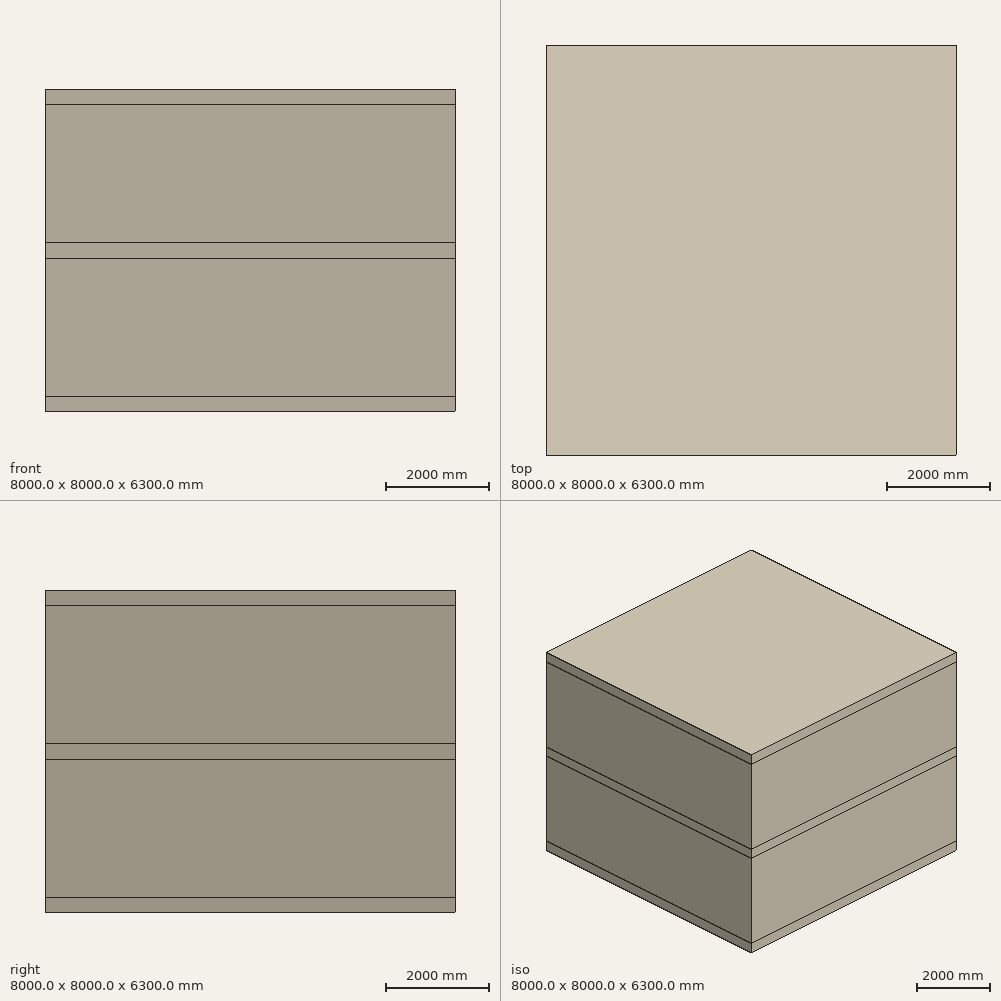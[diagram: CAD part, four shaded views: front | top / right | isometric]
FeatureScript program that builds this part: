
annotation { "Feature Type Name" : "Feature", "Feature Type Description" : "" }
export const myFeature = defineFeature(function(context is Context, id is Id, definition is map)
    precondition{}
    {
        {
            var Q0;
            Q0=qCreatedBy(makeId("Top.planeOp"),FACE);
            var sketch = newSketch(context, id + "F0", { "sketchPlane" : qUnion([Q0])});
            skLineSegment(sketch, "E0.bottom", {"start": v(4000, -4000) * mm, "end": v(-4000, -4000) * mm});
            skLineSegment(sketch, "E0.top", {"start": v(4000, 4000) * mm, "end": v(-4000, 4000) * mm});
            skLineSegment(sketch, "E0.left", {"start": v(4000, -4000) * mm, "end": v(4000, 4000) * mm});
            skLineSegment(sketch, "E0.right", {"start": v(-4000, -4000) * mm, "end": v(-4000, 4000) * mm});
            skPoint(sketch, "E0.middle", {"position": v(0, 0) * mm});
            skSolve(sketch);
        }
        {
            var Q0;
            Q0=qCreatedBy(makeId("Front.planeOp"),FACE);
            var sketch = newSketch(context, id + "F1", { "sketchPlane" : qUnion([Q0])});
            skLineSegment(sketch, "E1.bottom", {"start": v(-4000, 0) * mm, "end": v(4000, 0) * mm, "construction": true});
            skLineSegment(sketch, "E1.top", {"start": v(-4000, 3000) * mm, "end": v(4000, 3000) * mm, "construction": true});
            skLineSegment(sketch, "E1.left", {"start": v(-4000, 0) * mm, "end": v(-4000, 3000) * mm, "construction": true});
            skLineSegment(sketch, "E1.right", {"start": v(4000, 0) * mm, "end": v(4000, 3000) * mm, "construction": true});
            skLineSegment(sketch, "E2.top", {"start": v(-4000, 6000) * mm, "end": v(4000, 6000) * mm, "construction": true});
            skLineSegment(sketch, "E2.left", {"start": v(-4000, 3000) * mm, "end": v(-4000, 6000) * mm, "construction": true});
            skLineSegment(sketch, "E2.right", {"start": v(4000, 3000) * mm, "end": v(4000, 6000) * mm, "construction": true});
            skLineSegment(sketch, "E3.top", {"start": v(-4000, 9000) * mm, "end": v(4000, 9000) * mm, "construction": true});
            skLineSegment(sketch, "E3.left", {"start": v(-4000, 6000) * mm, "end": v(-4000, 9000) * mm, "construction": true});
            skLineSegment(sketch, "E3.right", {"start": v(4000, 6000) * mm, "end": v(4000, 9000) * mm, "construction": true});
            skSolve(sketch);
        }
        {
            var Q0;
            Q0=qCreatedBy(makeId("Top.planeOp"),FACE);
            var Q1;
            Q1=sQuery(id+"F1.wireOp",VERTEX,"E2.left.start");
            cPlane(context, id + "F2", {"entities" : qUnion([Q0, Q1]), "cplaneType" : CPlaneType.PLANE_POINT, "offset" : 25 * mm, "width" : 150 * mm, "height" : 150 * mm});
        }
        {
            var Q0;
            Q0=qCreatedBy(id+"F2.planeOp",FACE);
            var sketch = newSketch(context, id + "F3", { "sketchPlane" : qUnion([Q0])});
            skLineSegment(sketch, "E4.bottom", {"start": v(-4000, 4000) * mm, "end": v(4000, 4000) * mm});
            skLineSegment(sketch, "E4.top", {"start": v(-4000, -4000) * mm, "end": v(4000, -4000) * mm});
            skLineSegment(sketch, "E4.left", {"start": v(-4000, 4000) * mm, "end": v(-4000, -4000) * mm});
            skLineSegment(sketch, "E4.right", {"start": v(4000, 4000) * mm, "end": v(4000, -4000) * mm});
            skSolve(sketch);
        }
        {
            var Q0;
            Q0=qCreatedBy(makeId("Top.planeOp"),FACE);
            var Q1;
            Q1=sQuery(id+"F1.wireOp",VERTEX,"E2.left.end");
            cPlane(context, id + "F4", {"entities" : qUnion([Q0, Q1]), "cplaneType" : CPlaneType.PLANE_POINT, "offset" : 25 * mm, "width" : 150 * mm, "height" : 150 * mm});
        }
        {
            var Q0;
            Q0=qCreatedBy(id+"F4.planeOp",FACE);
            var sketch = newSketch(context, id + "F5", { "sketchPlane" : qUnion([Q0])});
            skLineSegment(sketch, "E5.bottom", {"start": v(-4000, 4000) * mm, "end": v(4000, 4000) * mm});
            skLineSegment(sketch, "E5.top", {"start": v(-4000, -4000) * mm, "end": v(4000, -4000) * mm});
            skLineSegment(sketch, "E5.left", {"start": v(-4000, 4000) * mm, "end": v(-4000, -4000) * mm});
            skLineSegment(sketch, "E5.right", {"start": v(4000, 4000) * mm, "end": v(4000, -4000) * mm});
            skSolve(sketch);
        }
        {
            var Q0;
            Q0=makeQuery(id+"F0.imprint","IMPRINT",FACE,{"disambiguationData":[TD([[makeQuery(id+"F0.imprint","IMPRINT",EDGE,{"derivedFrom":sQuery(id+"F0.wireOp",EDGE,"E0.bottom")}),-1.0]])]});
            var Q1;
            Q1=makeQuery(id+"F3.imprint","IMPRINT",FACE,{"disambiguationData":[TD([[makeQuery(id+"F3.imprint","IMPRINT",EDGE,{"derivedFrom":sQuery(id+"F3.wireOp",EDGE,"E4.bottom")}),-1.0]])]});
            var Q2;
            Q2=makeQuery(id+"F5.imprint","IMPRINT",FACE,{"disambiguationData":[TD([[makeQuery(id+"F5.imprint","IMPRINT",EDGE,{"derivedFrom":sQuery(id+"F5.wireOp",EDGE,"E5.bottom")}),-1.0]])]});
            extrude(context, id + "F6", {"entities" : qUnion([Q0, Q1, Q2]), "oppositeDirection" : true, "depth" : 300 * mm, "offsetDistance" : 25 * mm});
        }
        {
            var Q0;
            Q0=makeQuery(id+"F0.imprint","IMPRINT",FACE,{"disambiguationData":[TD([[makeQuery(id+"F0.imprint","IMPRINT",EDGE,{"derivedFrom":sQuery(id+"F0.wireOp",EDGE,"E0.bottom")}),-1.0]])]});
            var Q1;
            Q1=makeQuery(id+"F6.opExtrude","CAP_VERTEX",VERTEX,{"disambiguationData":[OSD([sQuery(id+"F3.wireOp",EDGE,"E4.top"),sQuery(id+"F3.wireOp",EDGE,"E4.left")])],"isStart":false});
            extrude(context, id + "F7", {"entities" : qUnion([Q0]), "endBound" : BoundingType.UP_TO_VERTEX, "depth" : 25 * mm, "endBoundEntityVertex" : qUnion([Q1]), "offsetDistance" : 25 * mm});
        }
        {
            var Q0;
            Q0=makeQuery(id+"F3.imprint","IMPRINT",FACE,{"disambiguationData":[TD([[makeQuery(id+"F3.imprint","IMPRINT",EDGE,{"derivedFrom":sQuery(id+"F3.wireOp",EDGE,"E4.bottom")}),-1.0]])]});
            var Q1;
            Q1=makeQuery(id+"F6.opExtrude","CAP_VERTEX",VERTEX,{"disambiguationData":[OSD([sQuery(id+"F5.wireOp",EDGE,"E5.top"),sQuery(id+"F5.wireOp",EDGE,"E5.left")])],"isStart":false});
            extrude(context, id + "F8", {"entities" : qUnion([Q0]), "endBound" : BoundingType.UP_TO_VERTEX, "depth" : 25 * mm, "endBoundEntityVertex" : qUnion([Q1]), "offsetDistance" : 25 * mm});
        }
    });
